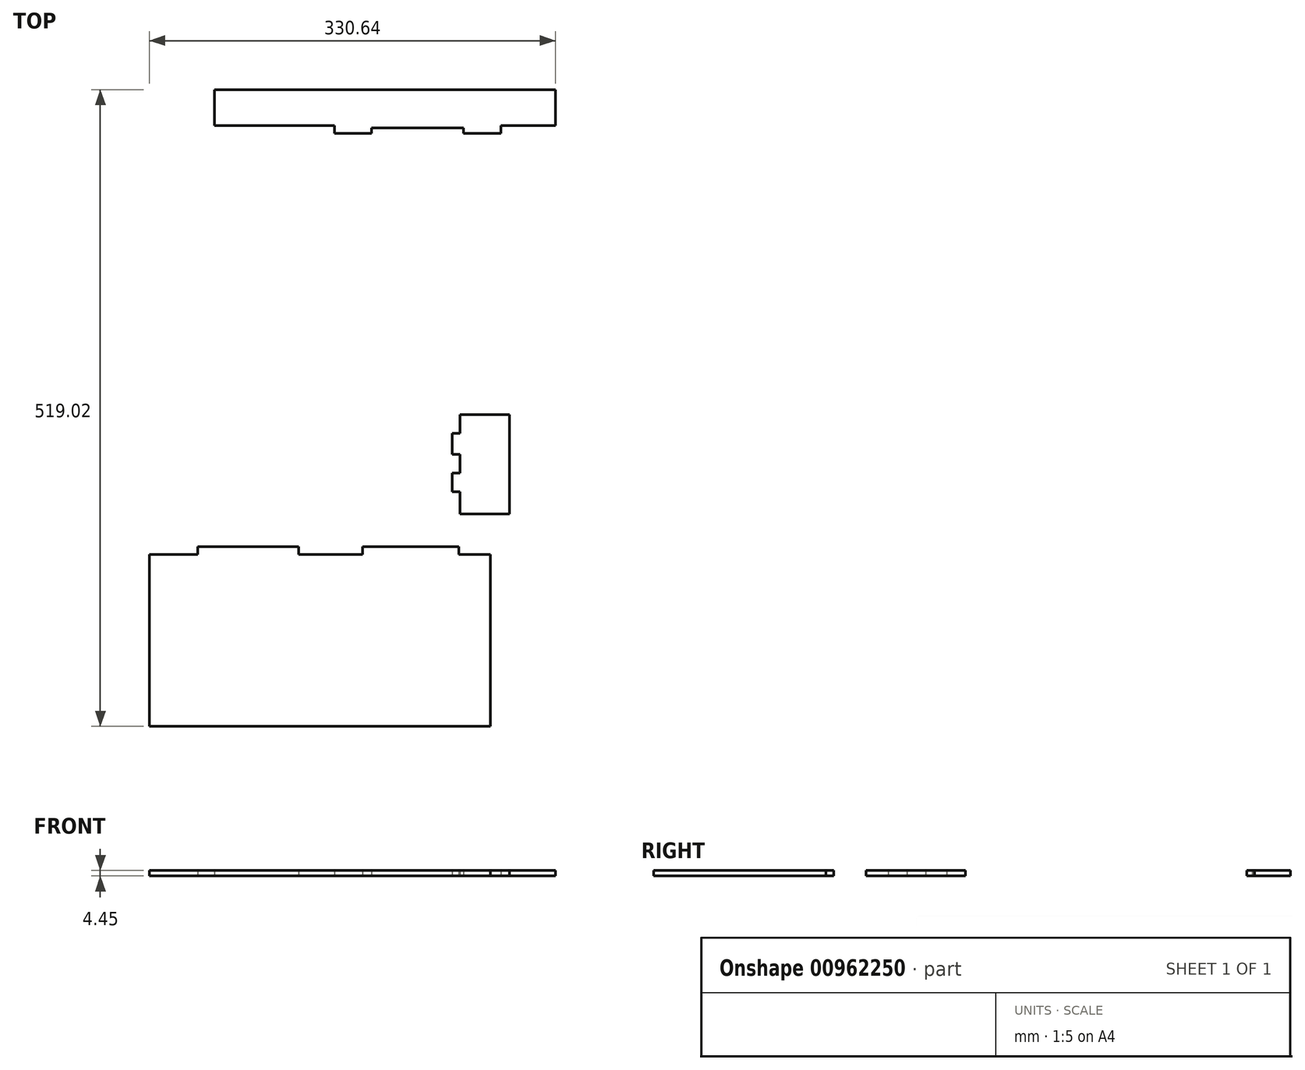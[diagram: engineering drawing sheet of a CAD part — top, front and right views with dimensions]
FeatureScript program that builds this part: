
annotation { "Feature Type Name" : "Feature", "Feature Type Description" : "" }
export const myFeature = defineFeature(function(context is Context, id is Id, definition is map)
    precondition{}
    {
        {
            var Q0;
            Q0=qCreatedBy(makeId("Top.planeOp"),FACE);
            var sketch = newSketch(context, id + "F0", { "sketchPlane" : qUnion([Q0])});
            skPoint(sketch, "E0.start.orphan", {"position": v(-23.94, -169.52) * mm});
            skLineSegment(sketch, "E1.bottom", {"start": v(-2.51, -185.75) * mm, "end": v(15.83, -185.75) * mm});
            skLineSegment(sketch, "E2.left", {"start": v(-80.35, -185.75) * mm, "end": v(-80.35, -201.04) * mm});
            skPoint(sketch, "E3.end.orphan", {"position": v(-48.56, -185.75) * mm});
            skLineSegment(sketch, "E4.bottom", {"start": v(45.83, -192.08) * mm, "end": v(15.83, -192.08) * mm});
            skPoint(sketch, "E4.middle", {"position": v(31.62, -185.75) * mm});
            skPoint(sketch, "E5.middle", {"position": v(159.6, -185.75) * mm});
            skPoint(sketch, "E4.top.end.orphan", {"position": v(17.41, -179.42) * mm});
            skPoint(sketch, "E6.orphan", {"position": v(47.41, -179.42) * mm});
            skPoint(sketch, "E5.top.end.orphan", {"position": v(142.34, -174.18) * mm});
            skPoint(sketch, "E7.orphan", {"position": v(176.85, -174.18) * mm});
            skLineSegment(sketch, "E8.bottom", {"start": v(152.59, -192.08) * mm, "end": v(122.59, -192.08) * mm});
            skLineSegment(sketch, "E8.left", {"start": v(152.59, -192.08) * mm, "end": v(152.58, -185.75) * mm});
            skLineSegment(sketch, "E8.right", {"start": v(122.59, -192.08) * mm, "end": v(122.58, -185.75) * mm});
            skLineSegment(sketch, "E9.trimOffspring", {"start": v(47.28, -185.75) * mm, "end": v(122.58, -185.75) * mm});
            skLineSegment(sketch, "E10.trimOffspring", {"start": v(152.58, -185.75) * mm, "end": v(199.85, -185.75) * mm});
            skPoint(sketch, "E11.middle", {"position": v(199.48, -209.33) * mm});
            skPoint(sketch, "E11.left.end.orphan", {"position": v(205.95, -200.47) * mm});
            skPoint(sketch, "E12.orphan", {"position": v(205.67, -218.2) * mm});
            skLineSegment(sketch, "E13.bottom", {"start": v(109.66, 43.6) * mm, "end": v(139.96, 43.6) * mm});
            skLineSegment(sketch, "E13.left", {"start": v(109.66, 43.6) * mm, "end": v(109.66, 49.94) * mm});
            skLineSegment(sketch, "E13.right", {"start": v(139.96, 43.6) * mm, "end": v(139.96, 48.06) * mm});
            skLineSegment(sketch, "E14.top", {"start": v(214.96, 43.6) * mm, "end": v(245.26, 43.6) * mm});
            skLineSegment(sketch, "E14.left", {"start": v(214.96, 48.06) * mm, "end": v(214.96, 43.6) * mm});
            skLineSegment(sketch, "E14.right", {"start": v(245.26, 49.94) * mm, "end": v(245.26, 43.6) * mm});
            skLineSegment(sketch, "E15", {"start": v(86.13, 49.94) * mm, "end": v(109.66, 49.94) * mm});
            skLineSegment(sketch, "E16", {"start": v(139.96, 48.06) * mm, "end": v(214.96, 48.06) * mm});
            skLineSegment(sketch, "E17", {"start": v(245.26, 49.94) * mm, "end": v(289.7, 49.94) * mm});
            skLineSegment(sketch, "E18.bottom", {"start": v(211.85, -185.75) * mm, "end": v(252.26, -185.75) * mm});
            skLineSegment(sketch, "E18.top", {"start": v(211.85, -266.77) * mm, "end": v(252.26, -266.77) * mm});
            skLineSegment(sketch, "E18.left", {"start": v(211.85, -185.75) * mm, "end": v(211.85, -200.65) * mm});
            skLineSegment(sketch, "E19.top", {"start": v(211.85, -218.2) * mm, "end": v(205.52, -218.2) * mm});
            skLineSegment(sketch, "E20.top", {"start": v(211.85, -248.5) * mm, "end": v(205.52, -248.5) * mm});
            skLineSegment(sketch, "E20.right", {"start": v(205.52, -233.2) * mm, "end": v(205.52, -248.5) * mm});
            skPoint(sketch, "E21.centerSnap0", {"position": v(211.85, -226.26) * mm});
            skLineSegment(sketch, "E22.trimOffspring", {"start": v(211.85, -218.2) * mm, "end": v(211.85, -226.26) * mm});
            skLineSegment(sketch, "E23.trimOffspring", {"start": v(211.85, -248.5) * mm, "end": v(211.85, -266.77) * mm});
            skPoint(sketch, "E24.start.orphan", {"position": v(58.75, -264.57) * mm});
            skLineSegment(sketch, "E25.right", {"start": v(-125.08, -185.75) * mm, "end": v(-125.08, -199.79) * mm});
            skLineSegment(sketch, "E26.MirrorCS", {"start": v(-125.08, -247.39) * mm, "end": v(-118.75, -247.39) * mm});
            skLineSegment(sketch, "E27.MirrorCS", {"start": v(-125.08, -217.09) * mm, "end": v(-118.75, -217.09) * mm});
            skLineSegment(sketch, "E28.MirrorCS", {"start": v(-125.08, -199.79) * mm, "end": v(-118.75, -199.79) * mm});
            skLineSegment(sketch, "E29.trimOffspring", {"start": v(-125.08, -247.39) * mm, "end": v(-125.08, -265.67) * mm});
            skLineSegment(sketch, "E30.trimOffspring", {"start": v(-125.08, -217.09) * mm, "end": v(-125.08, -228.74) * mm});
            skPoint(sketch, "E31.middle", {"position": v(0, -266.77) * mm});
            skPoint(sketch, "E32.orphan", {"position": v(-1.74, -273.1) * mm});
            skPoint(sketch, "E33.orphan", {"position": v(80.55, -273.1) * mm});
            skLineSegment(sketch, "E34.bottom", {"start": v(-40.94, -299.5) * mm, "end": v(-1.74, -299.5) * mm});
            skLineSegment(sketch, "E34.left", {"start": v(-40.94, -299.5) * mm, "end": v(-40.94, -439.76) * mm});
            skLineSegment(sketch, "E35.top", {"start": v(132.56, -293.17) * mm, "end": v(210.86, -293.17) * mm});
            skLineSegment(sketch, "E35.left", {"start": v(132.56, -299.5) * mm, "end": v(132.56, -293.17) * mm});
            skLineSegment(sketch, "E36.trimOffspring", {"start": v(80.56, -299.5) * mm, "end": v(132.56, -299.5) * mm});
            skLineSegment(sketch, "E37.trimOffspring", {"start": v(215.06, -299.5) * mm, "end": v(236.57, -299.5) * mm});
            skLineSegment(sketch, "E38", {"start": v(-118.75, -217.09) * mm, "end": v(-118.75, -199.79) * mm});
            skLineSegment(sketch, "E39", {"start": v(-118.75, -232.09) * mm, "end": v(-118.75, -247.39) * mm});
            skLineSegment(sketch, "E40.bottom", {"start": v(86.13, 49.94) * mm, "end": v(11.9, 49.94) * mm});
            skLineSegment(sketch, "E41", {"start": v(-64.44, -169.52) * mm, "end": v(-68.9, -169.52) * mm});
            skLineSegment(sketch, "E42", {"start": v(-23.94, -169.52) * mm, "end": v(-19.5, -169.52) * mm});
            skLineSegment(sketch, "E43.top", {"start": v(-1.74, -293.17) * mm, "end": v(80.56, -293.17) * mm});
            skLineSegment(sketch, "E43.left", {"start": v(-1.74, -299.5) * mm, "end": v(-1.74, -293.17) * mm});
            skLineSegment(sketch, "E43.right", {"start": v(80.56, -299.5) * mm, "end": v(80.56, -293.17) * mm});
            skLineSegment(sketch, "E44.MirrorCS", {"start": v(210.86, -293.17) * mm, "end": v(132.56, -293.17) * mm});
            skPoint(sketch, "E45.start.orphan", {"position": v(106.56, -299.5) * mm});
            skPoint(sketch, "E46.orphan", {"position": v(211.85, -232.77) * mm});
            skLineSegment(sketch, "E47", {"start": v(211.85, -218.2) * mm, "end": v(211.85, -230.2) * mm});
            skPoint(sketch, "E48.centerSnap0", {"position": v(-125.08, -222.91) * mm});
            skPoint(sketch, "E49.visualSharp", {"position": v(-6.11, -185.75) * mm});
            skArc(sketch, "E49.filletArc", {"start": v(-6.1, -184.23) * mm, "mid": v(-4.46, -185.35) * mm, "end": v(-2.51, -185.75) * mm});
            skLineSegment(sketch, "E50", {"start": v(45.83, -192.08) * mm, "end": v(45.83, -185.75) * mm});
            skLineSegment(sketch, "E51", {"start": v(15.83, -192.08) * mm, "end": v(15.83, -185.75) * mm});
            skLineSegment(sketch, "E52", {"start": v(16.32, -185.75) * mm, "end": v(15.83, -185.75) * mm});
            skLineSegment(sketch, "E53", {"start": v(-118.75, -232.09) * mm, "end": v(-125.08, -232.09) * mm});
            skLineSegment(sketch, "E54", {"start": v(-125.08, -232.09) * mm, "end": v(-125.08, -228.74) * mm});
            skPoint(sketch, "E55.middle", {"position": v(-69.63, -221.14) * mm});
            skPoint(sketch, "E55.middle.positionSnap0", {"position": v(-79.2, -221.14) * mm});
            skPoint(sketch, "E55.centerSnap0", {"position": v(-79.2, -221.14) * mm});
            skPoint(sketch, "E56.orphan", {"position": v(-79.2, -227.34) * mm});
            skPoint(sketch, "E57.MirrorCS.end.orphan", {"position": v(-74.72, -215.04) * mm});
            skPoint(sketch, "E57.MirrorCS.start.orphan", {"position": v(-79.2, -214.94) * mm});
            skLineSegment(sketch, "E58", {"start": v(-75.9, -230.97) * mm, "end": v(-75.9, -230.86) * mm});
            skLineSegment(sketch, "E59", {"start": v(-75.9, -215.57) * mm, "end": v(-75.9, -215.66) * mm});
            skLineSegment(sketch, "E60", {"start": v(-76.34, -243.08) * mm, "end": v(-76.34, -244.08) * mm});
            skLineSegment(sketch, "E61", {"start": v(215.06, -299.5) * mm, "end": v(210.86, -299.5) * mm});
            skLineSegment(sketch, "E62", {"start": v(210.86, -299.5) * mm, "end": v(210.86, -293.17) * mm});
            skLineSegment(sketch, "E63", {"start": v(236.57, -299.5) * mm, "end": v(236.57, -439.76) * mm});
            skPoint(sketch, "E64.MirrorCS.start.orphan", {"position": v(172.76, -266.77) * mm});
            skPoint(sketch, "E65.orphan", {"position": v(93.97, -266.77) * mm});
            skPoint(sketch, "E31.top.start.orphan", {"position": v(41.14, -260.44) * mm});
            skPoint(sketch, "E31.right.end.orphan", {"position": v(-41.14, -260.44) * mm});
            skLineSegment(sketch, "E66.bottom", {"start": v(-80.35, -266.77) * mm, "end": v(-40.94, -266.77) * mm});
            skLineSegment(sketch, "E67.top", {"start": v(93.36, -260.44) * mm, "end": v(171.36, -260.44) * mm});
            skLineSegment(sketch, "E67.left", {"start": v(93.36, -266.77) * mm, "end": v(93.36, -260.44) * mm});
            skLineSegment(sketch, "E68.trimOffspring", {"start": v(41.06, -266.77) * mm, "end": v(93.36, -266.77) * mm});
            skLineSegment(sketch, "E69.top", {"start": v(-40.94, -260.44) * mm, "end": v(41.06, -260.44) * mm});
            skLineSegment(sketch, "E69.left", {"start": v(-40.94, -266.77) * mm, "end": v(-40.94, -260.44) * mm});
            skLineSegment(sketch, "E69.right", {"start": v(41.06, -266.77) * mm, "end": v(41.06, -260.44) * mm});
            skLineSegment(sketch, "E70", {"start": v(171.36, -266.37) * mm, "end": v(171.36, -260.44) * mm});
            skLineSegment(sketch, "E71.left", {"start": v(-80.35, -185.14) * mm, "end": v(-80.35, -200.43) * mm});
            skLineSegment(sketch, "E72.MirrorCS", {"start": v(-74.02, -247.73) * mm, "end": v(-74.02, -232.73) * mm});
            skLineSegment(sketch, "E73.MirrorCS", {"start": v(-80.35, -200.43) * mm, "end": v(-74.02, -200.43) * mm});
            skLineSegment(sketch, "E74.trimOffspring", {"start": v(-80.35, -248.73) * mm, "end": v(-80.35, -267.01) * mm});
            skLineSegment(sketch, "E75", {"start": v(-80.35, -232.73) * mm, "end": v(-74.02, -232.73) * mm});
            skLineSegment(sketch, "E76", {"start": v(-74.02, -217.43) * mm, "end": v(-80.35, -217.43) * mm});
            skLineSegment(sketch, "E77", {"start": v(-80.35, -217.43) * mm, "end": v(-80.35, -232.73) * mm});
            skLineSegment(sketch, "E78", {"start": v(-74.02, -247.73) * mm, "end": v(-80.35, -247.73) * mm});
            skLineSegment(sketch, "E79", {"start": v(-80.35, -247.73) * mm, "end": v(-80.35, -248.73) * mm});
            skLineSegment(sketch, "E80", {"start": v(-74.02, -217.43) * mm, "end": v(-74.02, -200.43) * mm});
            skLineSegment(sketch, "E81", {"start": v(-80.35, -185.75) * mm, "end": v(-80.35, -184.23) * mm});
            skLineSegment(sketch, "E82", {"start": v(-80.35, -184.23) * mm, "end": v(-80.85, -184.23) * mm});
            skLineSegment(sketch, "E83", {"start": v(211.85, -230.2) * mm, "end": v(211.85, -232.77) * mm});
            skPoint(sketch, "E84.top.start.orphan", {"position": v(199.1, -232.77) * mm});
            skPoint(sketch, "E85.end.orphan", {"position": v(199.62, -233.2) * mm});
            skLineSegment(sketch, "E86", {"start": v(199.1, -232.77) * mm, "end": v(199.34, -232.77) * mm});
            skPoint(sketch, "E87.trimOffspring.end.orphan", {"position": v(198.57, -266.77) * mm});
            skPoint(sketch, "E84.bottom.end.orphan", {"position": v(193, -248.32) * mm});
            skPoint(sketch, "E84.bottom.start.orphan", {"position": v(198.86, -248.5) * mm});
            skLineSegment(sketch, "E88", {"start": v(171.36, -266.37) * mm, "end": v(199.48, -266.37) * mm});
            skLineSegment(sketch, "E89", {"start": v(199.48, -266.37) * mm, "end": v(199.48, -248.5) * mm});
            skLineSegment(sketch, "E90", {"start": v(199.48, -248.5) * mm, "end": v(193.15, -248.5) * mm});
            skLineSegment(sketch, "E91", {"start": v(193.15, -248.5) * mm, "end": v(193.15, -233.5) * mm});
            skPoint(sketch, "E11.right.start.orphan", {"position": v(193, -218.2) * mm});
            skPoint(sketch, "E92.start.orphan", {"position": v(193.29, -218.2) * mm});
            skPoint(sketch, "E11.top.end.orphan", {"position": v(193.29, -200.47) * mm});
            skPoint(sketch, "E11.top.start.orphan", {"position": v(199.62, -200.65) * mm});
            skLineSegment(sketch, "E93", {"start": v(199.85, -185.75) * mm, "end": v(199.85, -200.65) * mm});
            skLineSegment(sketch, "E94", {"start": v(193.15, -201.2) * mm, "end": v(193.15, -218.2) * mm});
            skLineSegment(sketch, "E95", {"start": v(205.52, -218.2) * mm, "end": v(205.52, -200.9) * mm});
            skLineSegment(sketch, "E96", {"start": v(205.52, -200.9) * mm, "end": v(211.85, -200.9) * mm});
            skLineSegment(sketch, "E97", {"start": v(211.85, -200.9) * mm, "end": v(211.85, -200.65) * mm});
            skPoint(sketch, "E19.bottom.end.orphan", {"position": v(205.52, -200.65) * mm});
            skLineSegment(sketch, "E98", {"start": v(205.52, -233.2) * mm, "end": v(211.85, -233.2) * mm});
            skLineSegment(sketch, "E99", {"start": v(211.85, -233.2) * mm, "end": v(211.85, -232.77) * mm});
            skLineSegment(sketch, "E100", {"start": v(193.15, -218.2) * mm, "end": v(199.48, -218.2) * mm});
            skLineSegment(sketch, "E101", {"start": v(199.48, -218.2) * mm, "end": v(199.48, -233.5) * mm});
            skLineSegment(sketch, "E102", {"start": v(199.48, -233.5) * mm, "end": v(193.15, -233.5) * mm});
            skLineSegment(sketch, "E103", {"start": v(45.83, -185.75) * mm, "end": v(47.28, -185.75) * mm});
            skLineSegment(sketch, "E104", {"start": v(193.15, -201.2) * mm, "end": v(199.85, -201.2) * mm});
            skLineSegment(sketch, "E105", {"start": v(199.85, -201.2) * mm, "end": v(199.85, -200.65) * mm});
            skLineSegment(sketch, "E106", {"start": v(-133.22, -185.75) * mm, "end": v(-133.22, -184.65) * mm});
            skPoint(sketch, "E107.orphan", {"position": v(-125.08, -184.65) * mm});
            skLineSegment(sketch, "E108", {"start": v(-125.08, -265.67) * mm, "end": v(-148.06, -265.67) * mm});
            skLineSegment(sketch, "E109", {"start": v(-148.06, -265.67) * mm, "end": v(-148.06, -185.75) * mm});
            skLineSegment(sketch, "E110", {"start": v(-148.06, -185.75) * mm, "end": v(-125.08, -185.75) * mm});
            skLineSegment(sketch, "E111", {"start": v(-80.35, -184.23) * mm, "end": v(-62.03, -184.23) * mm});
            skLineSegment(sketch, "E112", {"start": v(-62.03, -184.23) * mm, "end": v(-62.03, -266.77) * mm});
            skLineSegment(sketch, "E113", {"start": v(-62.03, -184.23) * mm, "end": v(-6.1, -184.23) * mm});
            skLineSegment(sketch, "E114", {"start": v(185.42, -266.37) * mm, "end": v(185.42, -185.75) * mm});
            skLineSegment(sketch, "E115", {"start": v(252.26, -185.75) * mm, "end": v(252.26, -266.77) * mm});
            skLineSegment(sketch, "E116", {"start": v(289.7, 79.26) * mm, "end": v(11.9, 79.26) * mm});
            skLineSegment(sketch, "E117", {"start": v(11.9, 49.94) * mm, "end": v(11.9, 79.26) * mm});
            skLineSegment(sketch, "E118", {"start": v(289.7, 79.26) * mm, "end": v(289.7, 49.94) * mm});
            skLineSegment(sketch, "E119", {"start": v(-40.94, -439.76) * mm, "end": v(236.57, -439.76) * mm});
            skSolve(sketch);
        }
        {
            var Q0;
            Q0=makeQuery(id+"F0.imprint","IMPRINT",FACE,{"disambiguationData":[TD([[makeQuery(id+"F0.imprint","IMPRINT",EDGE,{"derivedFrom":sQuery(id+"F0.wireOp",EDGE,"E34.bottom")}),-1.0]])]});
            var Q1;
            Q1=makeQuery(id+"F0.imprint","IMPRINT",FACE,{"disambiguationData":[TD([[makeQuery(id+"F0.imprint","IMPRINT",EDGE,{"derivedFrom":sQuery(id+"F0.wireOp",EDGE,"E25.bottom")}),-1.0]])]});
            var Q2;
            {var subQ4=sQuery(id+"F0.wireOp",EDGE,"sC4kQ6F8-xUsw-eNn1-kUFQ-Rawnznmu5okk");Q2=makeQuery(id+"F0.imprint","IMPRINT",FACE,{"disambiguationData":[TD([[makeQuery(id+"F0.imprint","IMPRINT",EDGE,{"derivedFrom":subQ4}),-1.0]])]});}
            var Q3;
            Q3=makeQuery(id+"F0.imprint","IMPRINT",FACE,{"disambiguationData":[TD([[makeQuery(id+"F0.imprint","IMPRINT",EDGE,{"derivedFrom":sQuery(id+"F0.wireOp",EDGE,"E18.bottom")}),-1.0]])]});
            var Q4;
            Q4=makeQuery(id+"F0.imprint","IMPRINT",FACE,{"disambiguationData":[TD([[makeQuery(id+"F0.imprint","IMPRINT",EDGE,{"derivedFrom":sQuery(id+"F0.wireOp",EDGE,"E13.bottom")}),1.0]])]});
            var Q5;
            Q5=makeQuery(id+"F0.imprint","IMPRINT",FACE,{"disambiguationData":[TD([[makeQuery(id+"F0.imprint","IMPRINT",EDGE,{"derivedFrom":sQuery(id+"F0.wireOp",EDGE,"8f7e70ec-829e-447a-bce2-bef464287ae05.MirrorCS")}),1.0]])]});
            var Q6;
            Q6=makeQuery(id+"F0.imprint","IMPRINT",FACE,{"disambiguationData":[TD([[makeQuery(id+"F0.imprint","IMPRINT",EDGE,{"derivedFrom":sQuery(id+"F0.wireOp",EDGE,"8f7e70ec-829e-447a-bce2-bef464287ae00.MirrorCS")}),1.0]])]});
            var Q7;
            Q7=makeQuery(id+"F0.imprint","IMPRINT",FACE,{"disambiguationData":[TD([[makeQuery(id+"F0.imprint","IMPRINT",EDGE,{"derivedFrom":sQuery(id+"F0.wireOp",EDGE,"8f7e70ec-829e-447a-bce2-bef464287ae022.MirrorCS")}),1.0]])]});
            var Q8;
            Q8=makeQuery(id+"F0.imprint","IMPRINT",FACE,{"disambiguationData":[TD([[makeQuery(id+"F0.imprint","IMPRINT",EDGE,{"derivedFrom":sQuery(id+"F0.wireOp",EDGE,"8f7e70ec-829e-447a-bce2-bef464287ae038.MirrorCS")}),1.0]])]});
            var Q9;
            Q9=makeQuery(id+"F0.imprint","IMPRINT",FACE,{"disambiguationData":[TD([[makeQuery(id+"F0.imprint","IMPRINT",EDGE,{"derivedFrom":sQuery(id+"F0.wireOp",EDGE,"c39d97be-4391-4180-8587-fc0a7e54e684.0")}),-1.0]])]});
            extrude(context, id + "F1", {"entities" : qUnion([Q0, Q1, Q2, Q3, Q4, Q5, Q6, Q7, Q8, Q9]), "depth" : 4.45 * mm, "offsetDistance" : 25 * mm});
        }
    });
